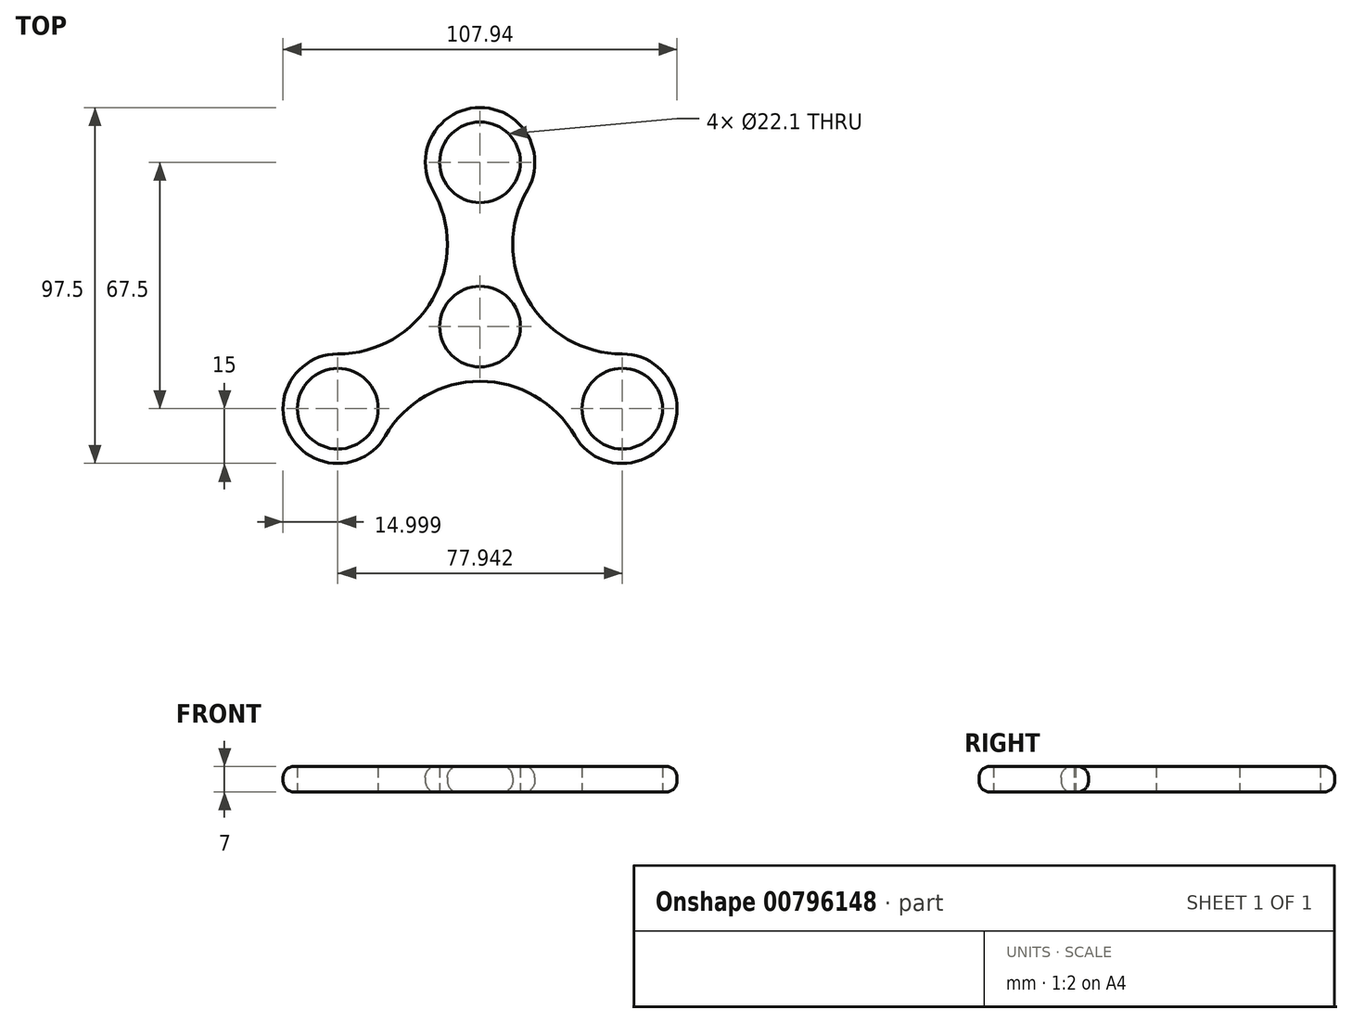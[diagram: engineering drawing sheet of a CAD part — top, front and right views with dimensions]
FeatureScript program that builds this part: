
annotation { "Feature Type Name" : "Feature", "Feature Type Description" : "" }
export const myFeature = defineFeature(function(context is Context, id is Id, definition is map)
    precondition{}
    {
        {
            var Q0;
            Q0=qCreatedBy(makeId("Top.planeOp"),FACE);
            var sketch = newSketch(context, id + "F0", { "sketchPlane" : qUnion([Q0])});
            skCircle(sketch, "E0", {"center": v(0, 0) * mm, "radius": 11.05 * mm});
            skLineSegment(sketch, "E1", {"start": v(0, 0) * mm, "end": v(0, 54.28) * mm, "construction": true});
            skLineSegment(sketch, "E2", {"start": v(0, 0) * mm, "end": v(-46.9, -27.08) * mm, "construction": true});
            skLineSegment(sketch, "E3", {"start": v(0, 0) * mm, "end": v(48, -27.71) * mm, "construction": true});
            skPoint(sketch, "E4", {"position": v(0, 45) * mm});
            skPoint(sketch, "E5", {"position": v(-38.97, -22.5) * mm});
            skPoint(sketch, "E6", {"position": v(38.97, -22.5) * mm});
            skCircle(sketch, "E7", {"center": v(-38.97, -22.5) * mm, "radius": 11.05 * mm});
            skCircle(sketch, "E8", {"center": v(0, 45) * mm, "radius": 11.05 * mm});
            skCircle(sketch, "E9", {"center": v(38.97, -22.5) * mm, "radius": 11.05 * mm});
            skCircle(sketch, "E10", {"center": v(0, 45) * mm, "radius": 15 * mm});
            skCircle(sketch, "E11", {"center": v(-38.97, -22.5) * mm, "radius": 15 * mm});
            skCircle(sketch, "E12", {"center": v(38.97, -22.5) * mm, "radius": 15 * mm});
            skLineSegment(sketch, "E13", {"start": v(0, 0) * mm, "end": v(45.24, 26.12) * mm, "construction": true});
            skLineSegment(sketch, "E14", {"start": v(0, 0) * mm, "end": v(-41.77, 24.12) * mm, "construction": true});
            skLineSegment(sketch, "E15", {"start": v(0, 0) * mm, "end": v(0, -53.8) * mm, "construction": true});
            skPoint(sketch, "E16", {"position": v(-38.97, 22.5) * mm});
            skPoint(sketch, "E17", {"position": v(38.97, 22.5) * mm});
            skPoint(sketch, "E18", {"position": v(0, -45) * mm});
            skArc(sketch, "E19", {"start": v(-44.45, -7) * mm, "mid": v(-13, 7.5) * mm, "end": v(-16.17, 42) * mm});
            skArc(sketch, "E20", {"start": v(16.17, 42) * mm, "mid": v(13, 7.5) * mm, "end": v(44.45, -7) * mm});
            skLineSegment(sketch, "E21", {"start": v(-28.28, -35) * mm, "end": v(-28.28, -35) * mm});
            skArc(sketch, "E22", {"start": v(28.28, -35) * mm, "mid": v(0, 45) * mm, "end": v(-28.28, -35) * mm, "construction": true});
            skArc(sketch, "E23", {"start": v(-28.28, -35) * mm, "mid": v(0, -45) * mm, "end": v(28.28, -35) * mm, "construction": true});
            skLineSegment(sketch, "E24", {"start": v(28.28, -35) * mm, "end": v(28.28, -35) * mm});
            skArc(sketch, "E25", {"start": v(28.28, -35) * mm, "mid": v(0, -15) * mm, "end": v(-28.28, -35) * mm});
            skSolve(sketch);
        }
        {
            var Q0;
            Q0=makeQuery(id+"F0.imprint","IMPRINT",FACE,{"disambiguationData":[TD([[makeQuery(id+"F0.imprint","IMPRINT",EDGE,{"derivedFrom":sQuery(id+"F0.wireOp",EDGE,"E7")}),-1.0]])]});
            var Q1;
            Q1=makeQuery(id+"F0.imprint","IMPRINT",FACE,{"disambiguationData":[TD([[makeQuery(id+"F0.imprint","IMPRINT",EDGE,{"derivedFrom":sQuery(id+"F0.wireOp",EDGE,"E0")}),-1.0]])]});
            var Q2;
            Q2=makeQuery(id+"F0.imprint","IMPRINT",FACE,{"disambiguationData":[TD([[makeQuery(id+"F0.imprint","IMPRINT",EDGE,{"derivedFrom":sQuery(id+"F0.wireOp",EDGE,"E8")}),-1.0]])]});
            var Q3;
            Q3=makeQuery(id+"F0.imprint","IMPRINT",FACE,{"disambiguationData":[TD([[makeQuery(id+"F0.imprint","IMPRINT",EDGE,{"derivedFrom":sQuery(id+"F0.wireOp",EDGE,"E9")}),-1.0]])]});
            extrude(context, id + "F1", {"entities" : qUnion([Q0, Q1, Q2, Q3]), "depth" : 7 * mm, "offsetDistance" : 25 * mm});
        }
        {
            var Q0;
            Q0=makeQuery(id+"F1.opExtrude","CAP_EDGE",EDGE,{"disambiguationData":[OSD([sQuery(id+"F0.wireOp",EDGE,"E11")])],"isStart":false});
            var Q1;
            Q1=makeQuery(id+"F1.opExtrude","CAP_EDGE",EDGE,{"disambiguationData":[OSD([sQuery(id+"F0.wireOp",EDGE,"E25")])],"isStart":true});
            fillet(context, id + "F2", {"entities" : qUnion([Q0, Q1]), "radius" : 3 * mm, "tangentPropagation" : true, "allowEdgeOverflow" : false});
        }
    });
